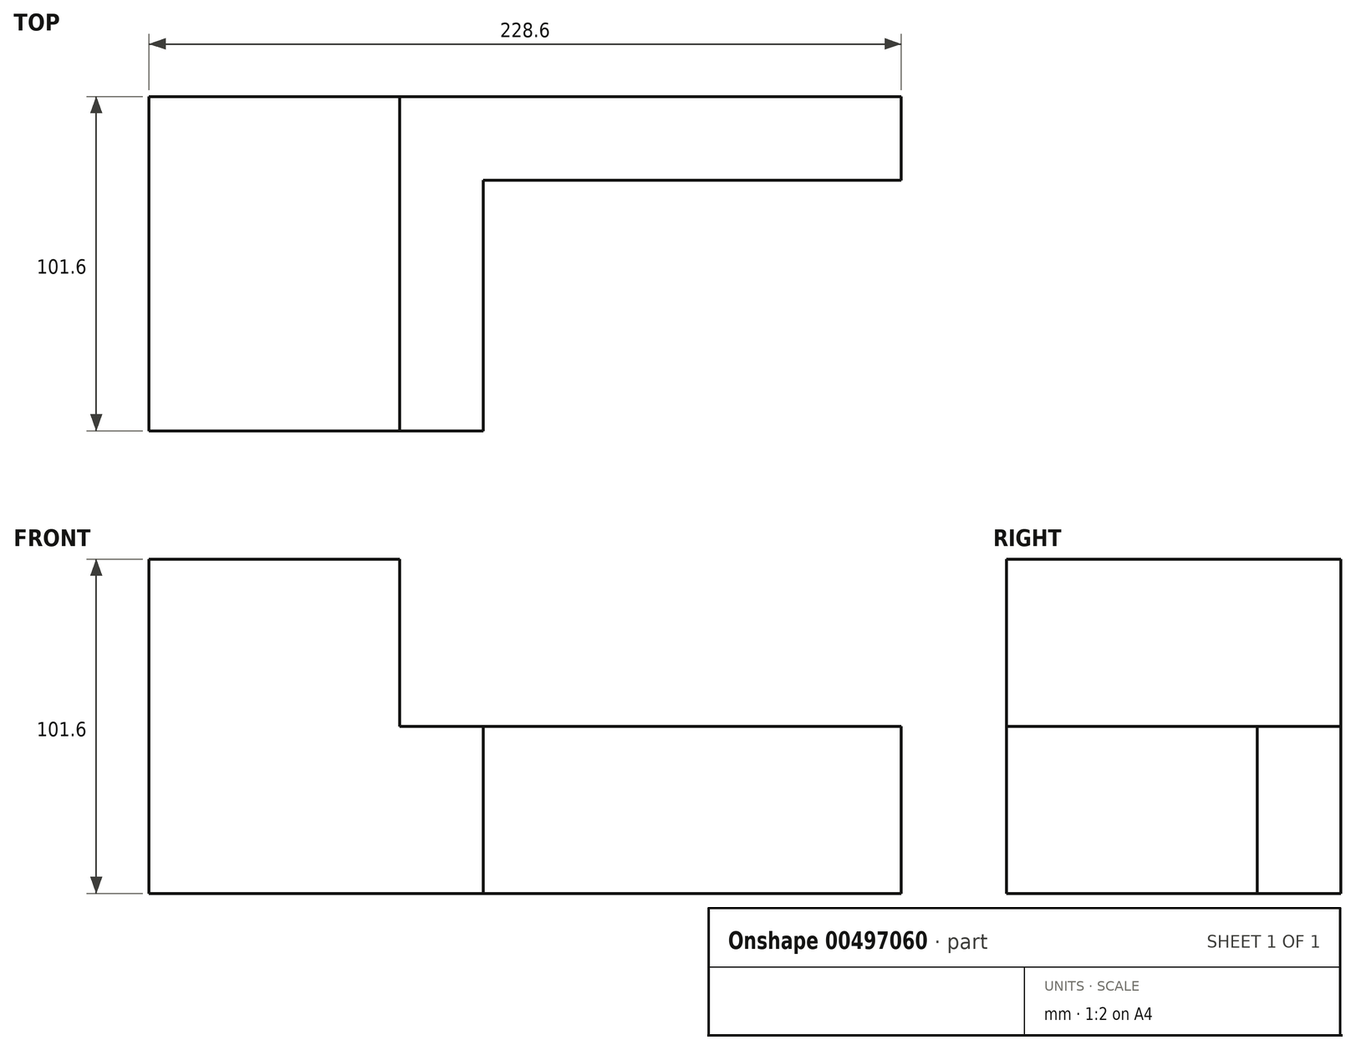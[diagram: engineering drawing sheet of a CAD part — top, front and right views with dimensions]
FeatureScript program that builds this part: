
annotation { "Feature Type Name" : "Feature", "Feature Type Description" : "" }
export const myFeature = defineFeature(function(context is Context, id is Id, definition is map)
    precondition{}
    {
        {
            var Q0;
            Q0=qCreatedBy(makeId("Front.planeOp"),FACE);
            var sketch = newSketch(context, id + "F0", { "sketchPlane" : qUnion([Q0])});
            skLineSegment(sketch, "E0.bottom", {"start": v(-40.72, 13.45) * mm, "end": v(60.88, 13.45) * mm});
            skLineSegment(sketch, "E0.top", {"start": v(-40.72, -37.35) * mm, "end": v(60.88, -37.35) * mm});
            skLineSegment(sketch, "E0.left", {"start": v(-40.72, 13.45) * mm, "end": v(-40.72, -37.35) * mm});
            skLineSegment(sketch, "E0.right", {"start": v(60.88, 13.45) * mm, "end": v(60.88, -37.35) * mm});
            skLineSegment(sketch, "E1.bottom", {"start": v(-40.72, 13.45) * mm, "end": v(35.48, 13.45) * mm});
            skLineSegment(sketch, "E1.top", {"start": v(-40.72, 64.25) * mm, "end": v(35.48, 64.25) * mm});
            skLineSegment(sketch, "E1.left", {"start": v(-40.72, 13.45) * mm, "end": v(-40.72, 64.25) * mm});
            skLineSegment(sketch, "E1.right", {"start": v(35.48, 13.45) * mm, "end": v(35.48, 64.25) * mm});
            skSolve(sketch);
        }
        {
            var Q0;
            Q0 = qSketchRegion(id + "F0", true);
            extrude(context, id + "F1", {"entities" : qUnion([Q0]), "depth" : 101.6 * mm});
        }
        {
            var Q0;
            Q0=makeQuery(id+"F1.opExtrude","SWEPT_FACE",FACE,{"disambiguationData":[OSD([sQuery(id+"F0.wireOp",EDGE,"E0.right")])]});
            var sketch = newSketch(context, id + "F2", { "sketchPlane" : qUnion([Q0])});
            skLineSegment(sketch, "E2.bottom", {"start": v(0, -37.35) * mm, "end": v(-25.4, -37.35) * mm});
            skLineSegment(sketch, "E2.top", {"start": v(0, 13.45) * mm, "end": v(-25.4, 13.45) * mm});
            skLineSegment(sketch, "E2.left", {"start": v(0, -37.35) * mm, "end": v(0, 13.45) * mm});
            skLineSegment(sketch, "E2.right", {"start": v(-25.4, -37.35) * mm, "end": v(-25.4, 13.45) * mm});
            skSolve(sketch);
        }
        {
            var Q0;
            Q0 = qSketchRegion(id + "F2", true);
            extrude(context, id + "F3", {"entities" : qUnion([Q0]), "operationType" : NewBodyOperationType.ADD, "depth" : 127 * mm});
        }
    });
